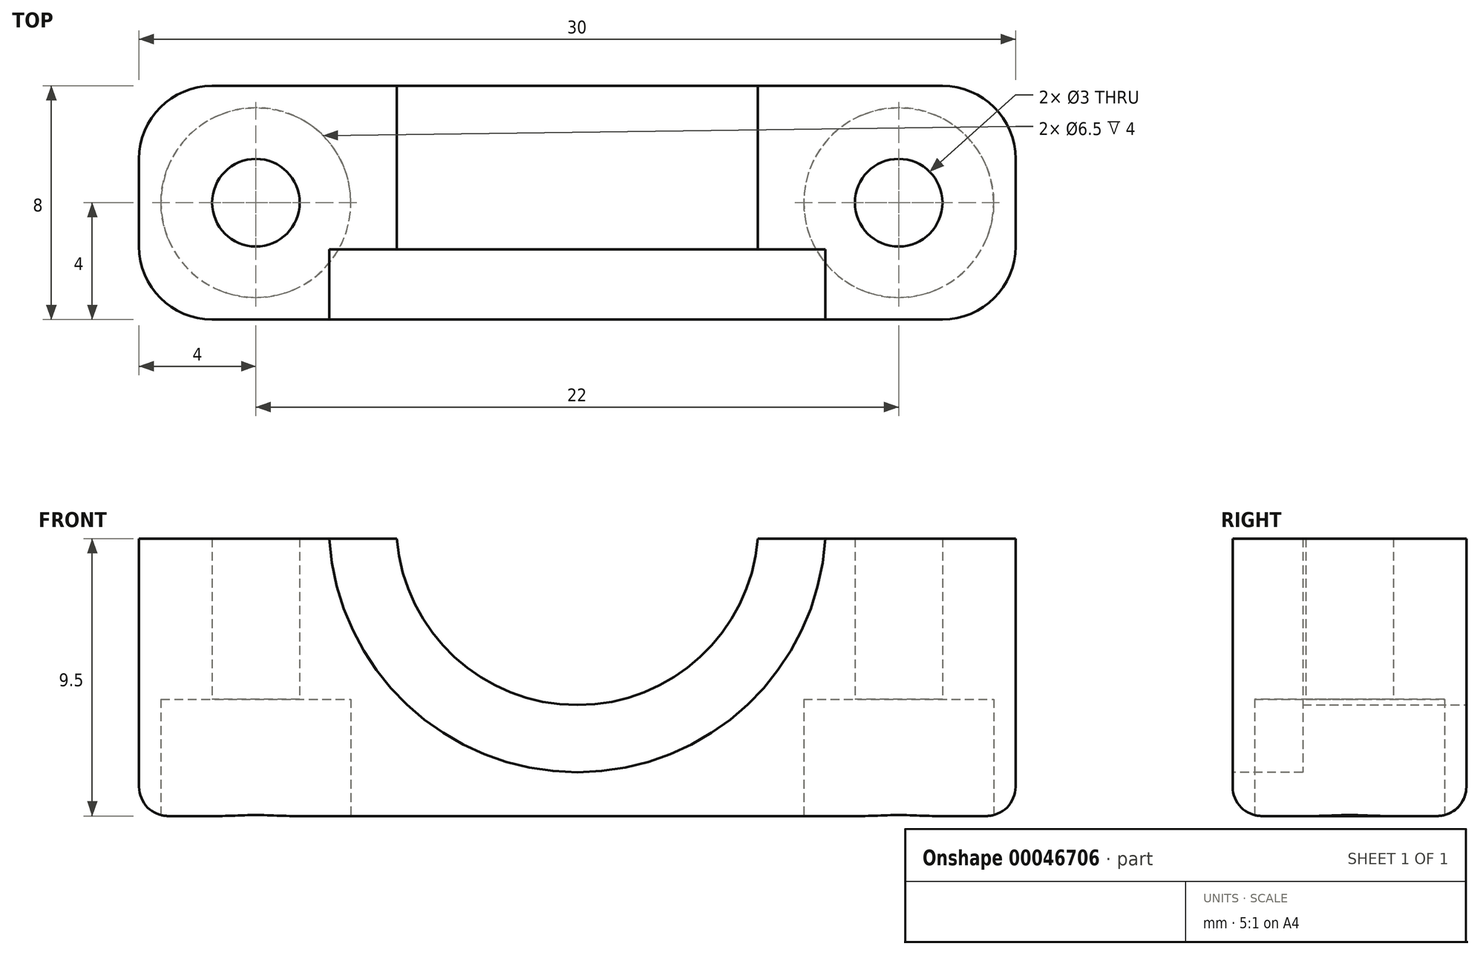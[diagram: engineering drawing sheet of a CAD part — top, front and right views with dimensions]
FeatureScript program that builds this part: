
annotation { "Feature Type Name" : "Feature", "Feature Type Description" : "" }
export const myFeature = defineFeature(function(context is Context, id is Id, definition is map)
    precondition{}
    {
        {
            var Q0;
            Q0=qCreatedBy(makeId("Top.planeOp"),FACE);
            var sketch = newSketch(context, id + "F0", { "sketchPlane" : qUnion([Q0])});
            skLineSegment(sketch, "E0", {"start": v(36.87, 0) * mm, "end": v(0, 0) * mm, "construction": true});
            skLineSegment(sketch, "E1", {"start": v(0, 0) * mm, "end": v(0, 29.7) * mm, "construction": true});
            skLineSegment(sketch, "E2.bottom", {"start": v(-15, 4) * mm, "end": v(15, 4) * mm});
            skLineSegment(sketch, "E2.top", {"start": v(-15, -4) * mm, "end": v(15, -4) * mm});
            skLineSegment(sketch, "E2.left", {"start": v(-15, 4) * mm, "end": v(-15, -4) * mm});
            skLineSegment(sketch, "E2.right", {"start": v(15, 4) * mm, "end": v(15, -4) * mm});
            skCircle(sketch, "E3", {"center": v(-11, 0) * mm, "radius": 1.5 * mm});
            skCircle(sketch, "E4", {"center": v(11, 0) * mm, "radius": 1.5 * mm});
            skSolve(sketch);
        }
        {
            var Q0;
            Q0=makeQuery(id+"F0.imprint","IMPRINT",FACE,{"disambiguationData":[TD([[makeQuery(id+"F0.imprint","IMPRINT",EDGE,{"derivedFrom":sQuery(id+"F0.wireOp",EDGE,"E2.bottom")}),-1.0]])]});
            extrude(context, id + "F1", {"entities" : qUnion([Q0]), "depth" : 10 * mm, "offsetDistance" : 25 * mm});
        }
        {
            var Q0;
            Q0=makeQuery(id+"F1.opExtrude","CAP_FACE",FACE,{"disambiguationData":[OSD([sQuery(id+"F0.wireOp",EDGE,"E2.bottom"),sQuery(id+"F0.wireOp",EDGE,"E2.top"),sQuery(id+"F0.wireOp",EDGE,"E2.left"),sQuery(id+"F0.wireOp",EDGE,"E2.right"),sQuery(id+"F0.wireOp",EDGE,"E3"),sQuery(id+"F0.wireOp",EDGE,"E4")])],"isStart":true});
            var sketch = newSketch(context, id + "F2", { "sketchPlane" : qUnion([Q0])});
            skCircle(sketch, "E5", {"center": v(11, 0) * mm, "radius": 3.25 * mm});
            skCircle(sketch, "E6", {"center": v(-11, 0) * mm, "radius": 3.25 * mm});
            skSolve(sketch);
        }
        {
            var Q0;
            Q0=makeQuery(id+"F2.imprint","IMPRINT",FACE,{"disambiguationData":[TD([[makeQuery(id+"F2.imprint","IMPRINT",EDGE,{"derivedFrom":sQuery(id+"F2.wireOp",EDGE,"E5")}),1.0]])]});
            var Q1;
            Q1=makeQuery(id+"F2.imprint","IMPRINT",FACE,{"disambiguationData":[TD([[makeQuery(id+"F2.imprint","IMPRINT",EDGE,{"derivedFrom":sQuery(id+"F2.wireOp",EDGE,"E6")}),1.0]])]});
            extrude(context, id + "F3", {"entities" : qUnion([Q0, Q1]), "operationType" : NewBodyOperationType.REMOVE, "oppositeDirection" : true, "depth" : 4 * mm, "offsetDistance" : 25 * mm});
        }
        {
            var Q0;
            Q0=makeQuery(id+"F1.opExtrude","SWEPT_FACE",FACE,{"disambiguationData":[OSD([sQuery(id+"F0.wireOp",EDGE,"E2.bottom")])]});
            var sketch = newSketch(context, id + "F4", { "sketchPlane" : qUnion([Q0])});
            skCircle(sketch, "E7", {"center": v(0, 10) * mm, "radius": 6.2 * mm});
            skSolve(sketch);
        }
        {
            var Q0;
            {var subQ0=sQuery(id+"F4.wireOp",EDGE,"E7");var subQ1=makeQuery(id+"F1.opExtrude","CAP_EDGE",EDGE,{"disambiguationData":[OSD([sQuery(id+"F0.wireOp",EDGE,"E2.bottom")])],"isStart":false});var subQ2=makeQuery(id+"F4.imprint","INTERSECT",VERTEX,{"disambiguationData":[OD(0.0)],"derivedFrom":[subQ1,subQ0]});Q0=makeQuery(id+"F4.imprint","IMPRINT",FACE,{"disambiguationData":[TD([[makeQuery(id+"F4.imprint","IMPRINT",EDGE,{"disambiguationData":[TD([[subQ2,1.0]])],"derivedFrom":subQ0}),1.0]])]});}
            extrude(context, id + "F5", {"entities" : qUnion([Q0]), "operationType" : NewBodyOperationType.REMOVE, "endBound" : BoundingType.THROUGH_ALL, "oppositeDirection" : true, "depth" : 25 * mm, "offsetDistance" : 25 * mm});
        }
        {
            var Q0;
            Q0=makeQuery(id+"F1.opExtrude","SWEPT_FACE",FACE,{"disambiguationData":[OSD([sQuery(id+"F0.wireOp",EDGE,"E2.top")])]});
            var sketch = newSketch(context, id + "F6", { "sketchPlane" : qUnion([Q0])});
            skCircle(sketch, "E8", {"center": v(0, 10) * mm, "radius": 8.5 * mm});
            skSolve(sketch);
        }
        {
            var Q0;
            {var subQ3=sQuery(id+"F0.wireOp",EDGE,"E2.top");var subQ5=makeQuery(id+"F5.opExtrude","SWEPT_FACE",FACE,{"disambiguationData":[OSD([sQuery(id+"F4.wireOp",EDGE,"E7")])]});var subQ6=makeQuery(id+"F1.opExtrude","SWEPT_FACE",FACE,{"disambiguationData":[OSD([subQ3])]});var subQ12=makeQuery(id+"F5.boolean.opBoolean","INTERSECT",EDGE,{"derivedFrom":[subQ6,subQ5]});Q0=makeQuery(id+"F6.imprint","IMPRINT",FACE,{"disambiguationData":[TD([[makeQuery(id+"F6.imprint","IMPRINT",EDGE,{"derivedFrom":subQ12}),1.0]])]});}
            extrude(context, id + "F7", {"entities" : qUnion([Q0]), "operationType" : NewBodyOperationType.REMOVE, "oppositeDirection" : true, "depth" : 2.4 * mm, "offsetDistance" : 25 * mm});
        }
        {
            var Q0;
            Q0=makeQuery(id+"F1.opExtrude","SWEPT_EDGE",EDGE,{"disambiguationData":[OSD([sQuery(id+"F0.wireOp",EDGE,"E2.bottom"),sQuery(id+"F0.wireOp",EDGE,"E2.right")])]});
            var Q1;
            Q1=makeQuery(id+"F1.opExtrude","SWEPT_EDGE",EDGE,{"disambiguationData":[OSD([sQuery(id+"F0.wireOp",EDGE,"E2.top"),sQuery(id+"F0.wireOp",EDGE,"E2.right")])]});
            var Q2;
            Q2=makeQuery(id+"F1.opExtrude","SWEPT_EDGE",EDGE,{"disambiguationData":[OSD([sQuery(id+"F0.wireOp",EDGE,"E2.bottom"),sQuery(id+"F0.wireOp",EDGE,"E2.left")])]});
            var Q3;
            Q3=makeQuery(id+"F1.opExtrude","SWEPT_EDGE",EDGE,{"disambiguationData":[OSD([sQuery(id+"F0.wireOp",EDGE,"E2.top"),sQuery(id+"F0.wireOp",EDGE,"E2.left")])]});
            fillet(context, id + "F8", {"entities" : qUnion([Q0, Q1, Q2, Q3]), "tangentPropagation" : true, "radius" : 2.5 * mm, "defaultsChanged" : false, "vertexSettings" : [], "allowEdgeOverflow" : false});
        }
        {
            var Q0;
            Q0=makeQuery(id+"F1.opExtrude","CAP_EDGE",EDGE,{"disambiguationData":[OSD([sQuery(id+"F0.wireOp",EDGE,"E2.right")])],"isStart":true});
            var Q1;
            Q1=makeQuery(id+"F1.opExtrude","CAP_EDGE",EDGE,{"disambiguationData":[OSD([sQuery(id+"F0.wireOp",EDGE,"E2.bottom")])],"isStart":true});
            var Q2;
            Q2=makeQuery(id+"F1.opExtrude","CAP_EDGE",EDGE,{"disambiguationData":[OSD([sQuery(id+"F0.wireOp",EDGE,"E2.left")])],"isStart":true});
            var Q3;
            Q3=makeQuery(id+"F1.opExtrude","CAP_EDGE",EDGE,{"disambiguationData":[OSD([sQuery(id+"F0.wireOp",EDGE,"E2.top")])],"isStart":true});
            fillet(context, id + "F9", {"entities" : qUnion([Q0, Q1, Q2, Q3]), "tangentPropagation" : true, "radius" : 1 * mm, "defaultsChanged" : true, "vertexSettings" : [], "allowEdgeOverflow" : false});
        }
        {
            var Q0;
            {var subQ0=sQuery(id+"F0.wireOp",EDGE,"E4");var subQ1=sQuery(id+"F0.wireOp",EDGE,"E2.top");var subQ2=sQuery(id+"F0.wireOp",EDGE,"E2.right");var subQ3=sQuery(id+"F0.wireOp",EDGE,"E2.bottom");Q0=makeQuery(id+"F5.boolean.opBoolean","SPLIT",FACE,{"disambiguationData":[TD([makeQuery(id+"F1.opExtrude","SWEPT_FACE",FACE,{"disambiguationData":[OSD([subQ2])]})])],"derivedFrom":makeQuery(id+"F1.opExtrude","CAP_FACE",FACE,{"disambiguationData":[OSD([subQ3,subQ1,sQuery(id+"F0.wireOp",EDGE,"E2.left"),subQ2,sQuery(id+"F0.wireOp",EDGE,"E3"),subQ0])],"isStart":false})});}
            var sketch = newSketch(context, id + "F10", { "sketchPlane" : qUnion([Q0])});
            skLineSegment(sketch, "E9.bottom", {"start": v(-17, 5.4) * mm, "end": v(18.45, 5.4) * mm});
            skLineSegment(sketch, "E9.top", {"start": v(-17, -6.23) * mm, "end": v(18.45, -6.23) * mm});
            skLineSegment(sketch, "E9.left", {"start": v(-17, 5.4) * mm, "end": v(-17, -6.23) * mm});
            skLineSegment(sketch, "E9.right", {"start": v(18.45, 5.4) * mm, "end": v(18.45, -6.23) * mm});
            skSolve(sketch);
        }
        {
            var Q0;
            Q0=makeQuery(id+"F10.imprint","IMPRINT",FACE,{"disambiguationData":[TD([[makeQuery(id+"F10.imprint","IMPRINT",EDGE,{"derivedFrom":sQuery(id+"F10.wireOp",EDGE,"E9.bottom")}),-1.0]])]});
            var Q1;
            {var subQ3=sQuery(id+"F0.wireOp",EDGE,"E4");Q1=makeQuery(id+"F10.imprint","IMPRINT",FACE,{"disambiguationData":[TD([[makeQuery(id+"F10.imprint","IMPRINT",EDGE,{"derivedFrom":makeQuery(id+"F1.opExtrude","CAP_EDGE",EDGE,{"disambiguationData":[OSD([subQ3])],"isStart":false})}),-1.0]])]});}
            extrude(context, id + "F11", {"entities" : qUnion([Q0, Q1]), "operationType" : NewBodyOperationType.REMOVE, "oppositeDirection" : true, "depth" : 0.5 * mm, "offsetDistance" : 25 * mm});
        }
    });
